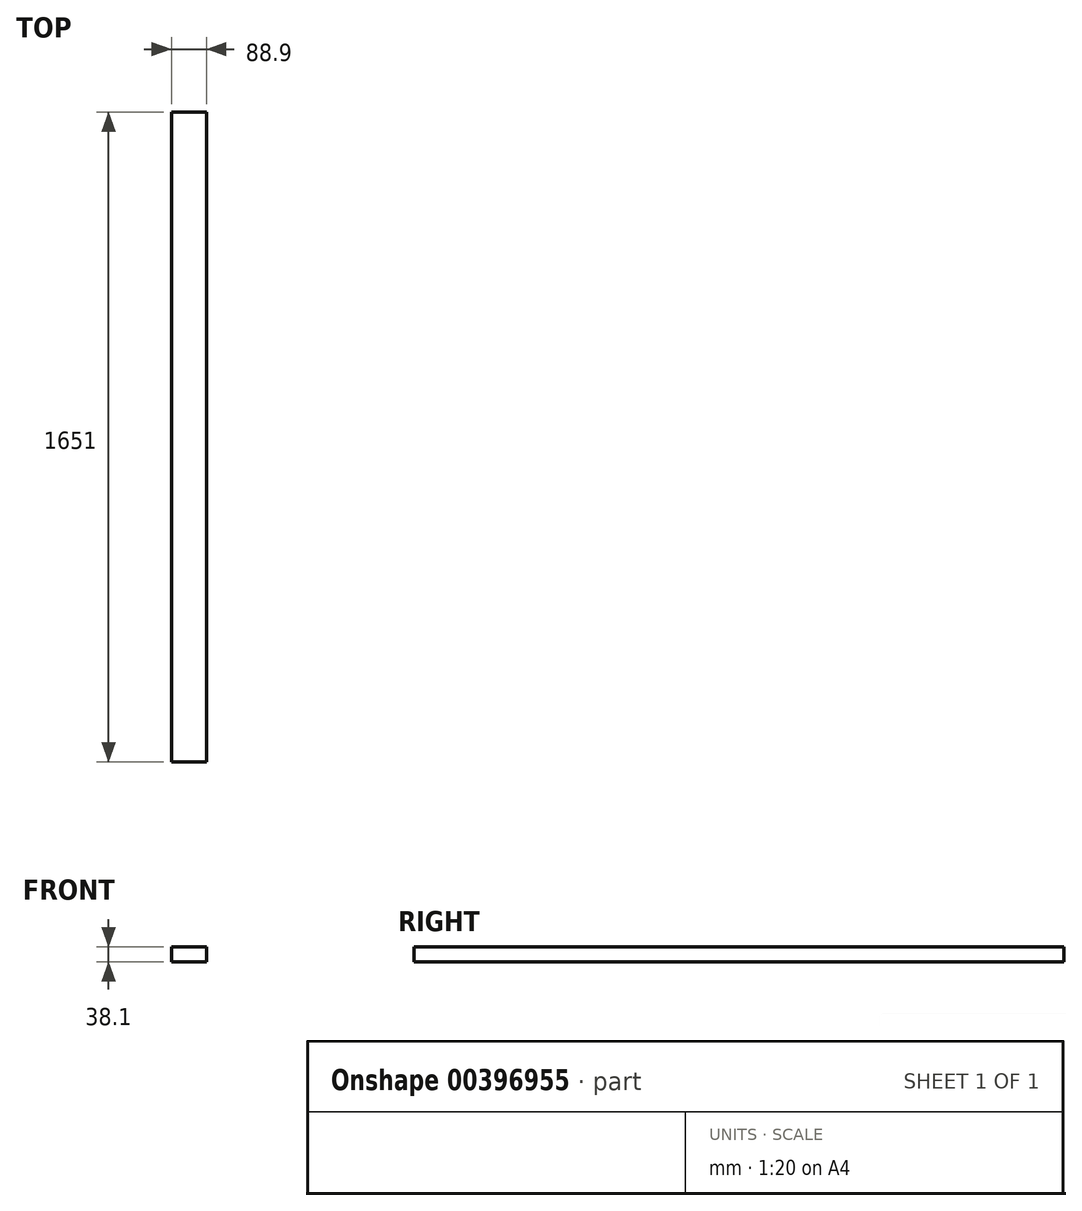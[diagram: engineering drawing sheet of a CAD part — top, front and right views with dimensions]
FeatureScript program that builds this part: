
annotation { "Feature Type Name" : "Feature", "Feature Type Description" : "" }
export const myFeature = defineFeature(function(context is Context, id is Id, definition is map)
    precondition{}
    {
        {
            var Q0;
            Q0=qCreatedBy(makeId("Front.planeOp"),FACE);
            var sketch = newSketch(context, id + "F0", { "sketchPlane" : qUnion([Q0])});
            skLineSegment(sketch, "E0.bottom", {"start": v(44.45, 19.05) * mm, "end": v(-44.45, 19.05) * mm});
            skLineSegment(sketch, "E0.top", {"start": v(44.45, -19.05) * mm, "end": v(-44.45, -19.05) * mm});
            skLineSegment(sketch, "E0.left", {"start": v(44.45, 19.05) * mm, "end": v(44.45, -19.05) * mm});
            skLineSegment(sketch, "E0.right", {"start": v(-44.45, 19.05) * mm, "end": v(-44.45, -19.05) * mm});
            skPoint(sketch, "E0.middle", {"position": v(0, 0) * mm});
            skSolve(sketch);
        }
        {
            var Q0;
            Q0=qSketchRegion(id+"F0",true);
            extrude(context, id + "F1", {"entities" : qUnion([Q0]), "depth" : 1651 * mm});
        }
    });
